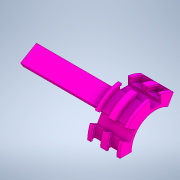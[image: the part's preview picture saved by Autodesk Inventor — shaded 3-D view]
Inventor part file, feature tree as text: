
AUTODESK INVENTOR PART (.ipt)
format: ipt  version: 2020 (Build 240168000, 168)  size: 210,944 bytes
history: native  units: mm
features: sketch x4, extrude x3, revolve x1
ambient origin geometry x8: Origin, YZ Plane, XZ Plane, XY Plane, X Axis, Y Axis, Z Axis, Center Point
bodies: Solid1 (feature_tree)
feature tree (8):
  extrude  "Extrusion1"  Depth=7.0mm
  extrude  "Extrusion2"  Depth=20.0mm TaperAngle=0.0deg
  revolve  "Revolution1"  [1 undecoded]
  extrude  "Extrusion3"  Depth=20.0mm TaperAngle=0.0deg
  sketch  "Sketch1"  dims[d0=15.0mm d1=7.0mm]
  sketch  "Sketch2"  dims[d2=120.0deg d3=20.0mm d4=0.0mm]
  sketch  "Sketch3"  dims[d5=6.2mm d6=17.0mm]
  sketch  "Sketch4"  dims[d7=10.0mm d8=20.0mm d9=0.0mm d10=10.0mm d11=1.0mm d12=1.0mm d13=1.0mm d14=1.0mm d15=1.0mm d16=2.5mm d17=20.594885mm d18=3.0mm d19=50.0mm d20=0.0mm d21=1.0mm d22=1.0mm d23=12.365244mm]
note: 1 required parameter value undecoded (feature->parameter linkage not recoverable at this tier; creation-order binding heuristic only, values carry confidence <= 0.55)
